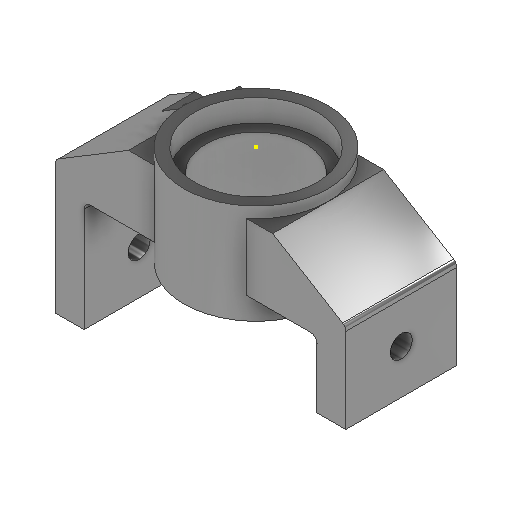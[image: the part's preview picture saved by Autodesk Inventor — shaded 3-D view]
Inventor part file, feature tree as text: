
AUTODESK INVENTOR PART (.ipt)
format: ipt  version: 2025.2 (Build 292293000, 293)  size: 239,616 bytes
history: native  units: mm
features: sketch x10, extrude x9, plane x1
ambient origin geometry x8: Origin, YZ Plane, XZ Plane, XY Plane, X Axis, Y Axis, Z Axis, Center Point
bodies: Solid1 (feature_tree)
feature tree (20):
  extrude  "Extrusion1"  Depth=30.0mm
  extrude  "Extrusion2"  Depth=30.0mm
  sketch  "Sketch3"  dims[d5=50.0mm d6=13.0mm]
  sketch  "Sketch4"  dims[d7=60.0mm d8=3.0mm]
  extrude  "Extrusion3"  Depth=13.0mm
  plane  "Work Plane1"
  extrude  "Extrusion4"  Depth=3.0mm
  extrude  "Extrusion5"  Depth=30.0mm
  extrude  "Extrusion6"  Depth=40.0mm
  extrude  "Extrusion7"  Depth=50.0mm TaperAngle=0.0deg
  extrude  "Extrusion8"  Depth=5.0mm TaperAngle=0.0deg
  extrude  "Extrusion9"  TaperAngle=0.0deg  [1 undecoded]
  sketch  "Sketch1"  dims[d0=65.0mm d1=30.0mm]
  sketch  "Sketch2"  dims[d3=10.0mm d4=30.0mm]
  sketch  "Sketch5"  dims[d10=20.0mm d11=30.0mm]
  sketch  "Sketch6"  dims[d12=13.0mm d13=40.0mm]
  sketch  "Sketch7"  dims[d14=3.0mm d15=50.0mm d16=0.0mm]
  sketch  "Sketch8"  dims[d17=65.0mm d18=5.0mm d19=40.0mm d20=0.0mm d21=0.0mm]
  sketch  "Sketch9"  dims[d22=55.0mm d23=0.0mm d24=0.0mm]
  sketch  "Sketch10"  dims[d25=-10.0mm d26=55.0mm d27=45.0mm d28=25.0mm d29=0.0mm d30=10.0mm d31=20.0mm d33=25.0mm d34=25.0mm d35=0.0mm d36=10.0mm d37=20.0mm d38=25.0mm d39=20.0mm d40=0.0mm d41=12.0mm d42=20.0mm d43=15.0mm d44=0.0mm d45=5.0mm d46=5.0mm d48=10.0mm d49=5.0mm d51=7.5mm d52=7.5mm d53=25.0mm d54=0.0mm d55=18.0mm d56=5.0mm d57=0.0mm d32=0.0mm]
note: 1 required parameter value undecoded (feature->parameter linkage not recoverable at this tier; creation-order binding heuristic only, values carry confidence <= 0.55)
